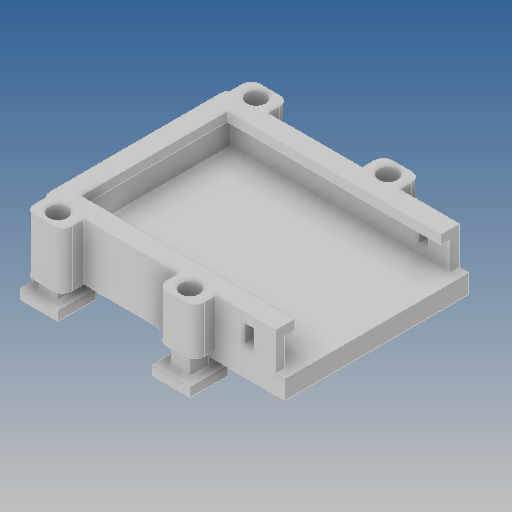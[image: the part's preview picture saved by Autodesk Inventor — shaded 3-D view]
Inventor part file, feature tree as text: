
AUTODESK INVENTOR PART (.ipt)
format: ipt  version: 2020 (Build 240168000, 168)  size: 327,168 bytes
history: native  units: mm
features: extrude x11, sketch x9, projected_geometry x5, other x2, fillet x2, pattern_linear x1, mirror x1
ambient origin geometry x8: Origin, YZ Plane, XZ Plane, XY Plane, X Axis, Y Axis, Z Axis, Center Point
bodies: Body1 (feature_tree)
feature tree (31):
  other  "DC-DC корпус"
  other  "Твердое тело1"
  sketch  "Эскиз1"
  extrude  "Выдавливание1"  Depth=23.0mm
  extrude  "Выдавливание2"  Depth=17.5mm
  extrude  "Выдавливание3"  Depth=1.0mm
  extrude  "Выдавливание4"  Depth=1.0mm TaperAngle=0.0deg
  extrude  "Выдавливание5"  Depth=3.0mm TaperAngle=0.0deg
  extrude  "Выдавливание6"  Depth=2.0mm
  extrude  "Выдавливание7"  Depth=2.0mm
  fillet  "Сопряжение1"  Radius=1.0mm
  sketch  "Эскиз8"
  extrude  "Выдавливание8"  Depth=1.0mm TaperAngle=0.0deg
  extrude  "Выдавливание9"  Depth=2.0mm
  extrude  "Выдавливание10"  Depth=2.0mm
  pattern_linear  "Прямоуг.массив2"  Spacing1=1.0mm  [1 undecoded]
  mirror  "Зеркальное отражение2"
  fillet  "Сопряжение3"  Radius=1.0mm
  extrude  "Выдавливание11"  Depth=1.0mm
  sketch  "Эскиз2"
  sketch  "Эскиз3"
  sketch  "Эскиз5"
  sketch  "Эскиз6"
  projected_geometry  "Спроецированная петля1"
  projected_geometry  "Спроецированная петля2"
  sketch  "Эскиз7"
  projected_geometry  "Спроецированная петля3"
  projected_geometry  "Спроецированная петля4"
  sketch  "Эскиз9"
  projected_geometry  "Спроецированная петля5"
  sketch  "Эскиз10"
note: 1 required parameter value undecoded (feature->parameter linkage not recoverable at this tier; creation-order binding heuristic only, values carry confidence <= 0.55)
